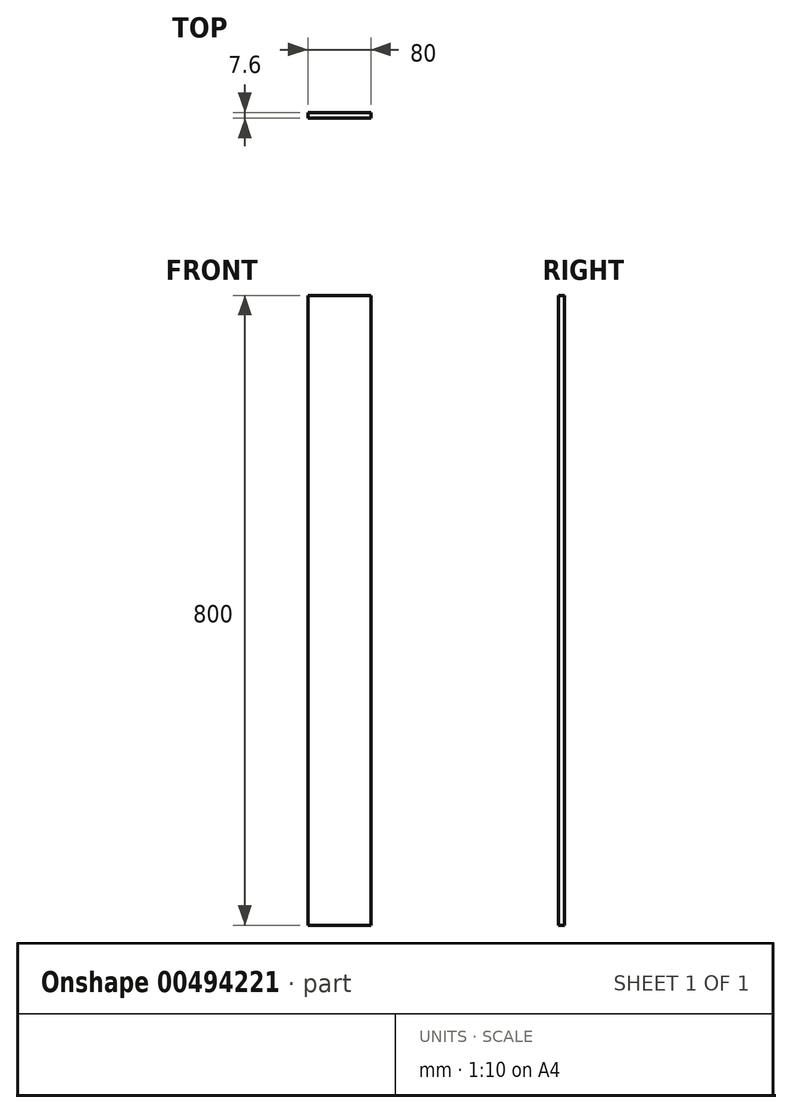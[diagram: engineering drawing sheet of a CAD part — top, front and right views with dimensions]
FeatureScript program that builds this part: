
annotation { "Feature Type Name" : "Feature", "Feature Type Description" : "" }
export const myFeature = defineFeature(function(context is Context, id is Id, definition is map)
    precondition{}
    {
        {
            var Q0;
            Q0=qCreatedBy(makeId("Front.planeOp"),FACE);
            var sketch = newSketch(context, id + "F0", { "sketchPlane" : qUnion([Q0])});
            skLineSegment(sketch, "E0.bottom", {"start": v(-48.46, 766.53) * mm, "end": v(31.54, 766.53) * mm});
            skLineSegment(sketch, "E0.top", {"start": v(-48.46, -33.47) * mm, "end": v(31.54, -33.47) * mm});
            skLineSegment(sketch, "E0.left", {"start": v(-48.46, 766.53) * mm, "end": v(-48.46, -33.47) * mm});
            skLineSegment(sketch, "E0.right", {"start": v(31.54, 766.53) * mm, "end": v(31.54, -33.47) * mm});
            skSolve(sketch);
        }
        {
            var Q0;
            Q0 = qSketchRegion(id + "F0", true);
            extrude(context, id + "F1", {"entities" : qUnion([Q0]), "depth" : 7.6 * mm});
        }
    });
